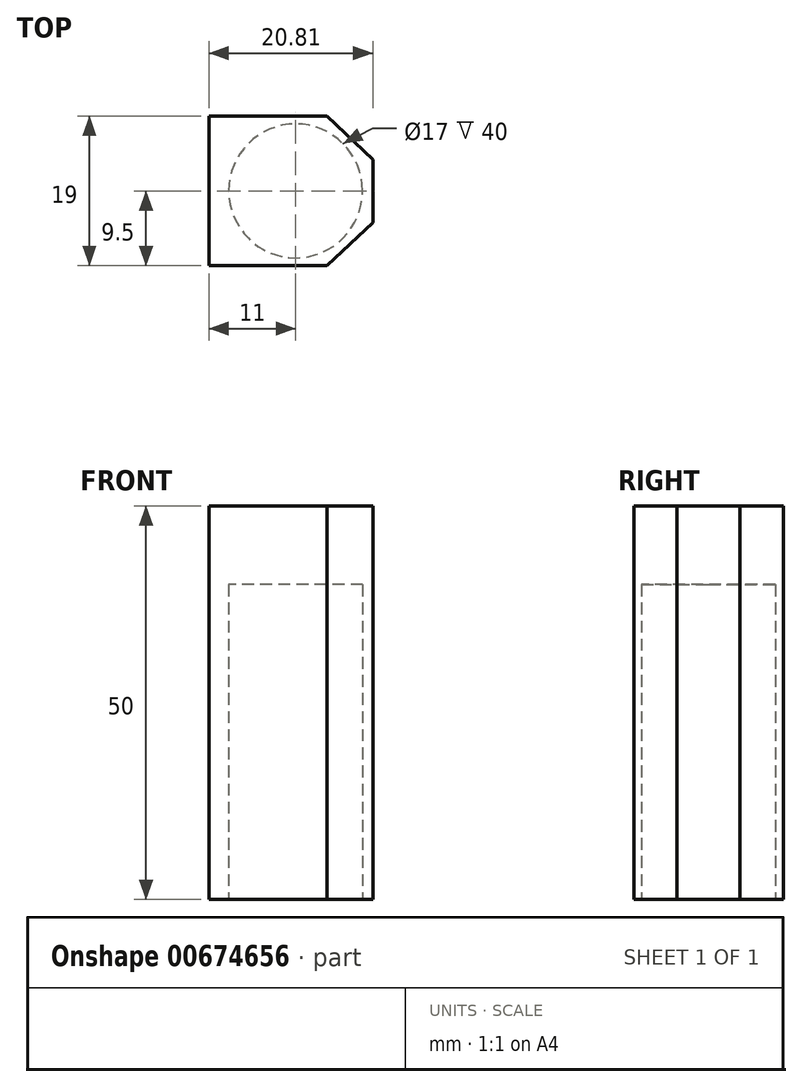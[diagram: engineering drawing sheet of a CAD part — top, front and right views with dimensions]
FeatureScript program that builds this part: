
annotation { "Feature Type Name" : "Feature", "Feature Type Description" : "" }
export const myFeature = defineFeature(function(context is Context, id is Id, definition is map)
    precondition{}
    {
        {
            var Q0;
            Q0=qCreatedBy(makeId("Top.planeOp"),FACE);
            var sketch = newSketch(context, id + "F0", { "sketchPlane" : qUnion([Q0])});
            skLineSegment(sketch, "E0", {"start": v(-13.35, 3.02) * mm, "end": v(1.65, 3.02) * mm});
            skLineSegment(sketch, "E1", {"start": v(1.65, 3.02) * mm, "end": v(7.46, -2.48) * mm});
            skLineSegment(sketch, "E2", {"start": v(7.46, -2.48) * mm, "end": v(7.46, -10.48) * mm});
            skLineSegment(sketch, "E3", {"start": v(7.46, -10.48) * mm, "end": v(1.65, -15.98) * mm});
            skLineSegment(sketch, "E4", {"start": v(1.65, -15.98) * mm, "end": v(-13.35, -15.98) * mm});
            skLineSegment(sketch, "E5", {"start": v(-13.35, -15.98) * mm, "end": v(-13.35, 3.02) * mm});
            skSolve(sketch);
        }
        {
            var Q0;
            Q0 = qSketchRegion(id + "F0", true);
            extrude(context, id + "F1", {"entities" : qUnion([Q0]), "depth" : 50 * mm, "offsetDistance" : 25.4 * mm});
        }
        {
            var Q0;
            Q0=qCreatedBy(makeId("Top.planeOp"),FACE);
            var sketch = newSketch(context, id + "F2", { "sketchPlane" : qUnion([Q0])});
            skCircle(sketch, "E6", {"center": v(-2.35, -6.48) * mm, "radius": 8.5 * mm});
            skSolve(sketch);
        }
        {
            var Q0;
            Q0 = qSketchRegion(id + "F2", true);
            extrude(context, id + "F3", {"entities" : qUnion([Q0]), "operationType" : NewBodyOperationType.REMOVE, "depth" : 40 * mm, "offsetDistance" : 25.4 * mm});
        }
    });
